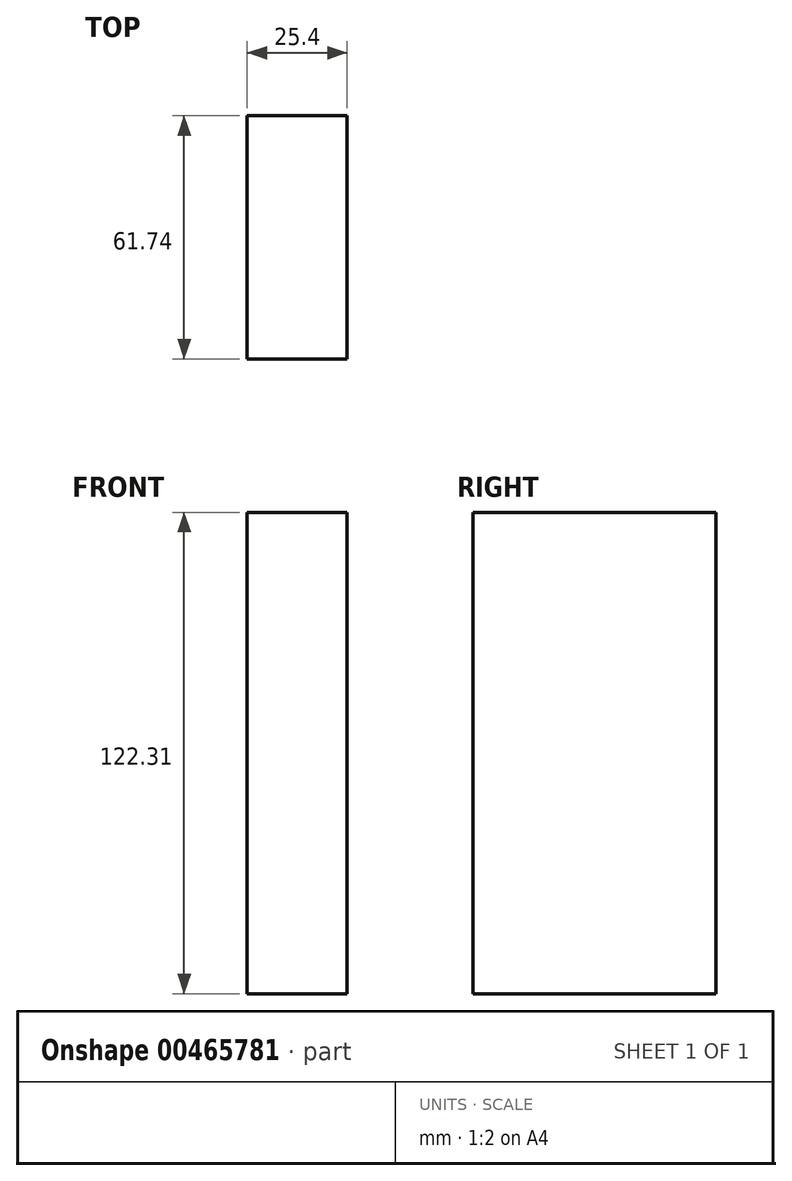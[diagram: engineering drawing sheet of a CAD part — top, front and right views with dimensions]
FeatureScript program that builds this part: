
annotation { "Feature Type Name" : "Feature", "Feature Type Description" : "" }
export const myFeature = defineFeature(function(context is Context, id is Id, definition is map)
    precondition{}
    {
        {
            var Q0;
            Q0=qCreatedBy(makeId("Right.planeOp"),FACE);
            var sketch = newSketch(context, id + "F0", { "sketchPlane" : qUnion([Q0])});
            skLineSegment(sketch, "E0.bottom", {"start": v(-61.74, -56.84) * mm, "end": v(0, -56.84) * mm});
            skLineSegment(sketch, "E0.top", {"start": v(-61.74, 65.47) * mm, "end": v(0, 65.47) * mm});
            skLineSegment(sketch, "E0.left", {"start": v(-61.74, -56.84) * mm, "end": v(-61.74, 65.47) * mm});
            skLineSegment(sketch, "E0.right", {"start": v(0, -56.84) * mm, "end": v(0, 65.47) * mm});
            skSolve(sketch);
        }
        {
            var Q0;
            Q0=makeQuery(id+"F0.imprint","IMPRINT",FACE,{"disambiguationData":[TD([[makeQuery(id+"F0.imprint","IMPRINT",EDGE,{"derivedFrom":sQuery(id+"F0.wireOp",EDGE,"E0.bottom")}),1.0]])]});
            extrude(context, id + "F1", {"entities" : qUnion([Q0]), "depth" : 25.4 * mm});
        }
    });
